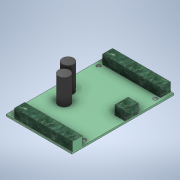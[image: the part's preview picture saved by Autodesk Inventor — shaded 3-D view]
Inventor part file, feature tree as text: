
AUTODESK INVENTOR PART (.ipt)
format: ipt  version: 2021 (Build 250183000, 183)  size: 163,328 bytes
history: native  units: mm
features: extrude x3, sketch x2, hole x1
ambient origin geometry x8: Origin, YZ Plane, XZ Plane, XY Plane, X Axis, Y Axis, Z Axis, Center Point
bodies: Solid1 (feature_tree)
feature tree (6):
  sketch  "Sketch1"  dims[d0=59.0mm d1=91.5mm]
  extrude  "Extrusion1"  Depth=91.5mm
  hole  "Hole1"  [1 undecoded]
  sketch  "Sketch2"  dims[d2=51.0mm d3=64.0mm d4=12.5mm d5=4.0mm d6=1.6mm d7=0.0mm d8=3.5mm d9=6.0mm d10=4.0mm d11=2.0mm d12=90.0deg d13=8.0mm d14=20.594885mm d15=10.0mm d16=10.0mm d18=46.0mm d19=9.5mm d20=35.0mm d21=17.0mm d22=52.0mm d23=9.0mm d24=7.0mm d25=9.5mm d26=52.0mm d27=9.0mm d28=9.5mm d29=4.5mm d30=9.0mm d31=12.0mm d32=9.5mm d33=48.0mm d34=23.0mm d35=0.0mm d36=8.0mm d37=0.0mm]
  extrude  "Extrusion2"  Depth=8.0mm
  extrude  "Extrusion3"  Depth=8.0mm
note: 1 required parameter value undecoded (feature->parameter linkage not recoverable at this tier; creation-order binding heuristic only, values carry confidence <= 0.55)
